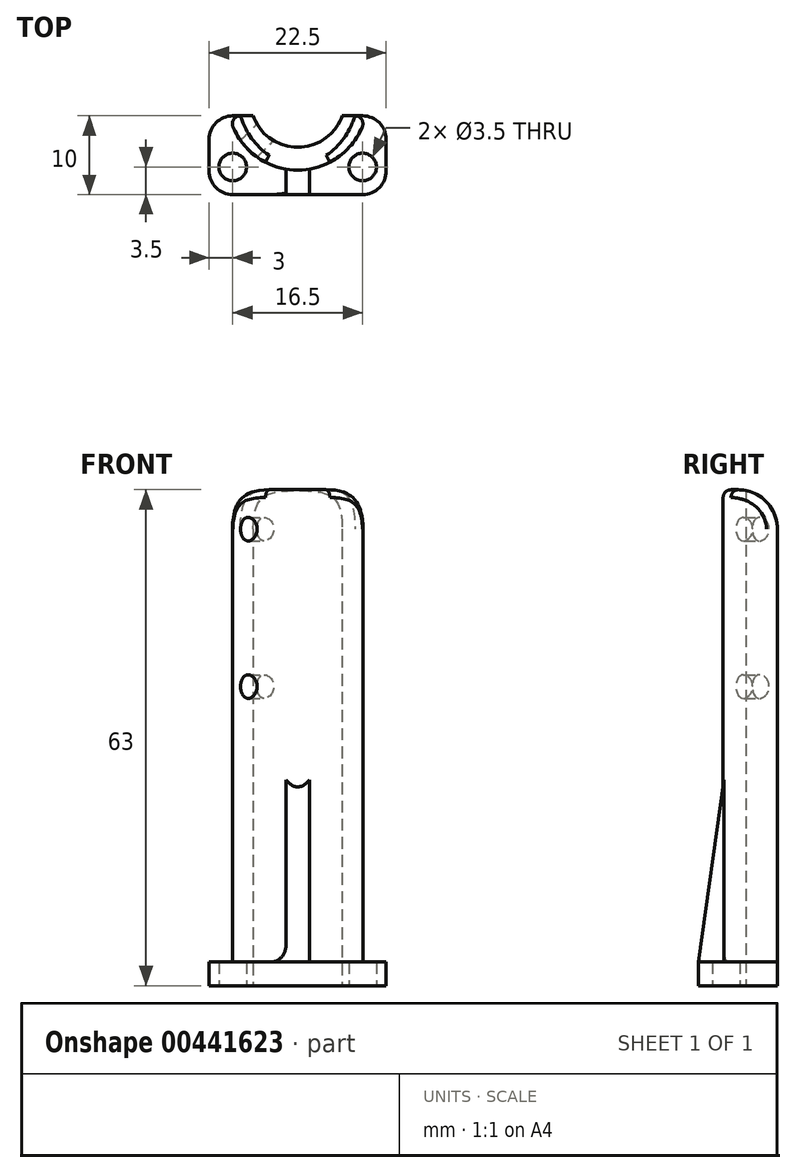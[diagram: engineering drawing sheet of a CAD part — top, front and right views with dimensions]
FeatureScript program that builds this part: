
annotation { "Feature Type Name" : "Feature", "Feature Type Description" : "" }
export const myFeature = defineFeature(function(context is Context, id is Id, definition is map)
    precondition{}
    {
        {
            var Q0;
            Q0=qCreatedBy(makeId("Top.planeOp"),FACE);
            var sketch = newSketch(context, id + "F0", { "sketchPlane" : qUnion([Q0])});
            skLineSegment(sketch, "E0", {"start": v(0, 0) * mm, "end": v(0, 18.16) * mm, "construction": true});
            skLineSegment(sketch, "E1", {"start": v(11.25, 0) * mm, "end": v(-11.25, 0) * mm});
            skLineSegment(sketch, "E2", {"start": v(-11.25, 0) * mm, "end": v(-11.25, 10) * mm});
            skLineSegment(sketch, "E3", {"start": v(-11.25, 10) * mm, "end": v(-8.25, 10) * mm});
            skLineSegment(sketch, "E4", {"start": v(11.25, 10) * mm, "end": v(11.25, 0) * mm});
            skLineSegment(sketch, "E5", {"start": v(-8.25, 0) * mm, "end": v(-8.25, 10) * mm, "construction": true});
            skLineSegment(sketch, "E6", {"start": v(8.25, 0) * mm, "end": v(8.25, 10) * mm, "construction": true});
            skCircle(sketch, "E7", {"center": v(-8.25, 3.5) * mm, "radius": 1.75 * mm});
            skCircle(sketch, "E8", {"center": v(8.25, 3.5) * mm, "radius": 1.75 * mm});
            skLineSegment(sketch, "E9", {"start": v(-8.25, 3.5) * mm, "end": v(8.25, 3.5) * mm, "construction": true});
            skCircle(sketch, "E10", {"center": v(0, 12) * mm, "radius": 6 * mm, "construction": true});
            skPoint(sketch, "E11.orphan", {"position": v(-5.25, 0) * mm});
            skArc(sketch, "E12", {"start": v(-5.66, 10) * mm, "mid": v(0, 6) * mm, "end": v(5.66, 10) * mm});
            skLineSegment(sketch, "E13.trimOffspring", {"start": v(5.66, 10) * mm, "end": v(11.25, 10) * mm});
            skLineSegment(sketch, "E14", {"start": v(-8.25, 10) * mm, "end": v(-5.66, 10) * mm});
            skSolve(sketch);
        }
        {
            var Q0;
            Q0=qSketchRegion(id+"F0",true);
            extrude(context, id + "F1", {"entities" : qUnion([Q0]), "depth" : 3 * mm});
        }
        {
            var Q0;
            Q0=makeQuery(id+"F1.opExtrude","CAP_FACE",FACE,{"disambiguationData":[OSD([sQuery(id+"F0.wireOp",EDGE,"As0BfuVP-EvKX-IIzB-8RFU-CAgbb2jAcoWc"),sQuery(id+"F0.wireOp",EDGE,"L4OFp0fu-src7-8fQ3-r4xW-09PvagWeFecp"),sQuery(id+"F0.wireOp",EDGE,"D5aVDjwy-oaWC-XehB-VUHR-Bb3EUq3Xvnb7"),sQuery(id+"F0.wireOp",EDGE,"E1"),sQuery(id+"F0.wireOp",EDGE,"E2"),sQuery(id+"F0.wireOp",EDGE,"E3"),sQuery(id+"F0.wireOp",EDGE,"E4"),sQuery(id+"F0.wireOp",EDGE,"Iq0820Bf-KlZ2-tIK3-RNVn-SmXuxhuQHUvB"),sQuery(id+"F0.wireOp",EDGE,"E7"),sQuery(id+"F0.wireOp",EDGE,"E8")])],"isStart":false});
            var sketch = newSketch(context, id + "F2", { "sketchPlane" : qUnion([Q0])});
            skArc(sketch, "E15.0", {"start": v(-5.66, 10) * mm, "mid": v(0, 6) * mm, "end": v(5.66, 10) * mm});
            skLineSegment(sketch, "E16", {"start": v(-5.66, 10) * mm, "end": v(-8.66, 10) * mm});
            skLineSegment(sketch, "E17", {"start": v(5.66, 10) * mm, "end": v(8.66, 10) * mm});
            skArc(sketch, "E18", {"start": v(-8.66, 10) * mm, "mid": v(0, 3.12) * mm, "end": v(8.66, 10) * mm});
            skSolve(sketch);
        }
        {
            var Q0;
            Q0=qSketchRegion(id+"F2",true);
            extrude(context, id + "F3", {"entities" : qUnion([Q0]), "operationType" : NewBodyOperationType.ADD, "depth" : 60 * mm});
        }
        {
            var Q0;
            Q0=makeQuery(id+"F1.opExtrude","CAP_FACE",FACE,{"disambiguationData":[OSD([sQuery(id+"F0.wireOp",EDGE,"E1"),sQuery(id+"F0.wireOp",EDGE,"E2"),sQuery(id+"F0.wireOp",EDGE,"E3"),sQuery(id+"F0.wireOp",EDGE,"E4"),sQuery(id+"F0.wireOp",EDGE,"E7"),sQuery(id+"F0.wireOp",EDGE,"E8"),sQuery(id+"F0.wireOp",EDGE,"E12"),sQuery(id+"F0.wireOp",EDGE,"E13.trimOffspring"),sQuery(id+"F0.wireOp",EDGE,"E14")])],"isStart":false});
            var sketch = newSketch(context, id + "F4", { "sketchPlane" : qUnion([Q0])});
            skLineSegment(sketch, "E19", {"start": v(0, 0) * mm, "end": v(0, 3.12) * mm, "construction": true});
            skLineSegment(sketch, "E20", {"start": v(0, 0) * mm, "end": v(1.5, 0) * mm});
            skLineSegment(sketch, "E21", {"start": v(1.5, 0) * mm, "end": v(1.5, 3.24) * mm});
            skLineSegment(sketch, "E22", {"start": v(0, 0) * mm, "end": v(-1.5, 0) * mm});
            skLineSegment(sketch, "E23", {"start": v(-1.5, 0) * mm, "end": v(-1.5, 3.24) * mm});
            skArc(sketch, "E24.0", {"start": v(-1.5, 3.24) * mm, "mid": v(0, 3.12) * mm, "end": v(1.5, 3.24) * mm});
            skPoint(sketch, "E25.orphan", {"position": v(-8.66, 10) * mm});
            skPoint(sketch, "E26.orphan", {"position": v(8.66, 10) * mm});
            skSolve(sketch);
        }
        {
            var Q0;
            Q0=qSketchRegion(id+"F4",true);
            extrude(context, id + "F5", {"entities" : qUnion([Q0]), "operationType" : NewBodyOperationType.ADD, "depth" : 25 * mm});
        }
        {
            var Q0;
            Q0=makeQuery(id+"F5.opExtrude","CAP_EDGE",EDGE,{"disambiguationData":[OSD([sQuery(id+"F4.wireOp",EDGE,"E20"),sQuery(id+"F4.wireOp",EDGE,"E22")])],"isStart":false});
            chamfer(context, id + "F6", {"entities" : qUnion([Q0]), "chamferType" : ChamferType.TWO_OFFSETS, "width1" : 25 * mm, "oppositeDirection" : false, "width2" : 3.5 * mm, "tangentPropagation" : true});
        }
        {
            var Q0;
            Q0=makeQuery(id+"F3.opExtrude","CAP_EDGE",EDGE,{"disambiguationData":[OSD([sQuery(id+"F2.wireOp",EDGE,"E17")])],"isStart":false});
            fillet(context, id + "F7", {"entities" : qUnion([Q0]), "radius" : 5 * mm, "tangentPropagation" : true, "allowEdgeOverflow" : false});
        }
        {
            var Q0;
            Q0=makeQuery(id+"F5.opExtrude","CAP_EDGE",EDGE,{"disambiguationData":[OSD([sQuery(id+"F4.wireOp",EDGE,"E21")])],"isStart":true});
            var Q1;
            Q1=makeQuery(id+"F5.opExtrude","CAP_EDGE",EDGE,{"disambiguationData":[OSD([sQuery(id+"F4.wireOp",EDGE,"E23")])],"isStart":true});
            fillet(context, id + "F8", {"entities" : qUnion([Q0, Q1]), "radius" : 2 * mm, "tangentPropagation" : true, "allowEdgeOverflow" : false});
        }
        {
            var Q0;
            Q0=makeQuery(id+"F1.opExtrude","SWEPT_EDGE",EDGE,{"disambiguationData":[OSD([sQuery(id+"F0.wireOp",EDGE,"E1"),sQuery(id+"F0.wireOp",EDGE,"E2")])]});
            var Q1;
            Q1=makeQuery(id+"F1.opExtrude","SWEPT_EDGE",EDGE,{"disambiguationData":[OSD([sQuery(id+"F0.wireOp",EDGE,"E1"),sQuery(id+"F0.wireOp",EDGE,"E4")])]});
            var Q2;
            Q2=makeQuery(id+"F1.opExtrude","SWEPT_EDGE",EDGE,{"disambiguationData":[OSD([sQuery(id+"F0.wireOp",EDGE,"E4"),sQuery(id+"F0.wireOp",EDGE,"E13.trimOffspring")])]});
            var Q3;
            Q3=makeQuery(id+"F1.opExtrude","SWEPT_EDGE",EDGE,{"disambiguationData":[OSD([sQuery(id+"F0.wireOp",EDGE,"E2"),sQuery(id+"F0.wireOp",EDGE,"E3")])]});
            fillet(context, id + "F9", {"entities" : qUnion([Q0, Q1, Q2, Q3]), "radius" : 3 * mm, "tangentPropagation" : true, "allowEdgeOverflow" : false});
        }
        {
            var Q0;
            Q0=makeQuery(id+"F3.opExtrude","CAP_EDGE",EDGE,{"disambiguationData":[OSD([sQuery(id+"F2.wireOp",EDGE,"E18")])],"isStart":false});
            fillet(context, id + "F10", {"entities" : qUnion([Q0]), "radius" : 1 * mm, "tangentPropagation" : true, "allowEdgeOverflow" : false});
        }
        {
            var Q0;
            Q0=qCreatedBy(makeId("Top.planeOp"),FACE);
            var sketch = newSketch(context, id + "F11", { "sketchPlane" : qUnion([Q0])});
            skArc(sketch, "E27.0", {"start": v(-5.66, 10) * mm, "mid": v(0, 6) * mm, "end": v(5.66, 10) * mm, "construction": true});
            skLineSegment(sketch, "E28", {"start": v(0, 12) * mm, "end": v(4.24, 7.76) * mm, "construction": true});
            skLineSegment(sketch, "E29", {"start": v(4.24, 7.76) * mm, "end": v(0, 12) * mm, "construction": true});
            skLineSegment(sketch, "E30", {"start": v(0, 12) * mm, "end": v(-4.24, 7.76) * mm, "construction": true});
            skLineSegment(sketch, "E31", {"start": v(0, 12) * mm, "end": v(0, 8.53) * mm, "construction": true});
            skSolve(sketch);
        }
        {
            var Q0;
            Q0=sQuery(id+"F11.wireOp",EDGE,"E30");
            var Q1;
            Q1=qCreatedBy(makeId("Front.planeOp"),FACE);
            cPlane(context, id + "F12", {"entities" : qUnion([Q0, Q1]), "cplaneType" : CPlaneType.LINE_ANGLE, "offset" : 25 * mm, "angle" : 0 * degree, "width" : 150 * mm, "height" : 150 * mm});
        }
        {
            var Q0;
            Q0=sQuery(id+"F11.wireOp",EDGE,"E29");
            var Q1;
            Q1=qCreatedBy(makeId("Front.planeOp"),FACE);
            cPlane(context, id + "F13", {"entities" : qUnion([Q0, Q1]), "cplaneType" : CPlaneType.LINE_ANGLE, "offset" : 25 * mm, "angle" : 0 * degree, "width" : 150 * mm, "height" : 150 * mm});
        }
        {
            var Q0;
            Q0=qCreatedBy(id+"F13.planeOp",FACE);
            var sketch = newSketch(context, id + "F14", { "sketchPlane" : qUnion([Q0])});
            skPoint(sketch, "E32.0", {"position": v(8.49, 0) * mm});
            skLineSegment(sketch, "E33", {"start": v(8.49, 0) * mm, "end": v(8.49, 58) * mm, "construction": true});
            skCircle(sketch, "E34", {"center": v(8.49, 58) * mm, "radius": 1.5 * mm});
            skCircle(sketch, "E35", {"center": v(8.49, 38) * mm, "radius": 1.5 * mm});
            skSolve(sketch);
        }
        {
            var Q0;
            Q0=qSketchRegion(id+"F14",true);
            extrude(context, id + "F15", {"entities" : qUnion([Q0]), "operationType" : NewBodyOperationType.REMOVE, "endBound" : BoundingType.THROUGH_ALL, "oppositeDirection" : true, "depth" : 25 * mm});
        }
        {
            var Q0;
            Q0=qCreatedBy(id+"F12.planeOp",FACE);
            var sketch = newSketch(context, id + "F16", { "sketchPlane" : qUnion([Q0])});
            skPoint(sketch, "E36.0", {"position": v(-8.49, 0) * mm});
            skLineSegment(sketch, "E37", {"start": v(-8.49, 0) * mm, "end": v(-8.49, 38.07) * mm, "construction": true});
            skSolve(sketch);
        }
    });
